# Revit family: xxxFloor_Drain-Linear-Whitehall_Manufacturing-BestCare-WHLVD_Series.rfaxxx
name_source: partatom
category: Plumbing Fixtures
units: mm (PartAtom-declared; Revit-internal decimal feet)

## family parameters
Cut with Voids When Loaded = Yes
Host = Face
OmniClass Number = 23.45.55.21
OmniClass Title = Drains (Wastes)
Part Type = Normal
Room Calculation Point = No
Round Connector Dimension = Use Diameter
Shared = No

## types (4) — shared parameters
Assembly Code = D2030300
CW Connection = No
Compliance Certifications = Member of U.S. Green Building Council, Recyclable ProductMember of U.S. Green Building Council, Recyclable Product
Default Elevation = 2"
Description = BestCare® Ligature-Resistant Linear Drain for Vinyl Floor
Finish = Stainless Steel-Whitehall Mfg-Satin
HW Connection = No
Height = 4 7/8"
Installation Instruction Link = https://www.whitehallmfg.com
Installation Type = Floor Mounted
Manufacturer = Whitehall Manufacturing
Materials = Stainless Steel-Whitehall Mfg-Satin
Outlet Diameter Connection = 2"
Product Documentation Link = https://www.whitehallmfg.com
Product Page URL = https://www.whitehallmfg.com
URL = https://www.whitehallmfg.com
Vent Connection = No
Waste Connection = Yes
zero-valued in all types: CWFU, HWFU, WFU

## per-type parameters (varying)
| type | A | A/2 | Open Area | WHLVD-12 12” Linear Vinyl Clamping Drain | WHLVD-24 24” Linear Vinyl Clamping Drain | WHLVD-36 36” Linear Vinyl Clamping Drain | WHLVD-48 48” Linear Vinyl Clamping Drain |
| WHLVD-12 | 12" | 3" | 3.00 sq. in. | Yes | No | No | No |
| WHLVD-24 | 24" | 6" | 5.90 sq. in. | No | Yes | No | No |
| WHLVD-36 | 36" | 9" | 9.27 sq. in. | No | No | Yes | No |
| WHLVD-48 | 48" | 12" | 12.50 sq. in. | No | No | No | Yes |

note: column(s) folded — value = type name in every type: Model

## geometry (parser evidence)
native form markers: Sweep x1
no freeform markers — native parametric forms only
